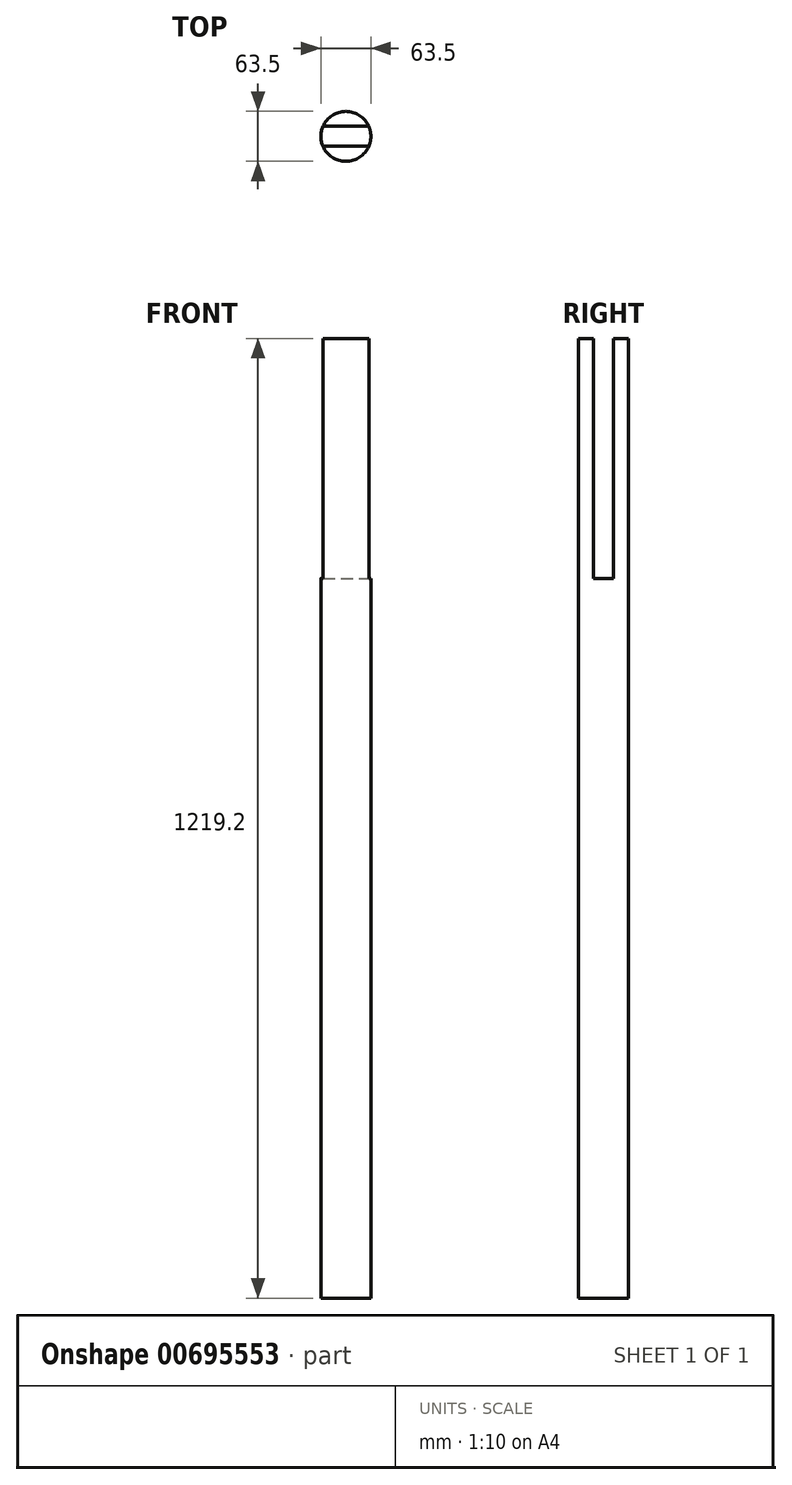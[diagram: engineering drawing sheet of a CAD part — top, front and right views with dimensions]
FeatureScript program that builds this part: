
annotation { "Feature Type Name" : "Feature", "Feature Type Description" : "" }
export const myFeature = defineFeature(function(context is Context, id is Id, definition is map)
    precondition{}
    {
        {
            var Q0;
            Q0=qCreatedBy(makeId("Top.planeOp"),FACE);
            var sketch = newSketch(context, id + "F0", { "sketchPlane" : qUnion([Q0])});
            skCircle(sketch, "E0", {"center": v(0, 0) * mm, "radius": 31.75 * mm});
            skSolve(sketch);
        }
        {
            var Q0;
            Q0 = qSketchRegion(id + "F0", true);
            extrude(context, id + "F1", {"entities" : qUnion([Q0]), "endBound" : BoundingType.SYMMETRIC, "oppositeDirection" : true, "depth" : 1219.2 * mm, "offsetDistance" : 25.4 * mm});
        }
        {
            var Q0;
            Q0=makeQuery(id+"F1.opExtrude","CAP_FACE",FACE,{"disambiguationData":[OSD([sQuery(id+"F0.wireOp",EDGE,"E0")])],"isStart":true});
            var sketch = newSketch(context, id + "F2", { "sketchPlane" : qUnion([Q0])});
            skLineSegment(sketch, "E1.bottom", {"start": v(-29.1, 12.7) * mm, "end": v(29.1, 12.7) * mm});
            skLineSegment(sketch, "E1.top", {"start": v(-29.1, -12.7) * mm, "end": v(29.1, -12.7) * mm});
            skPoint(sketch, "E1.middle", {"position": v(0, 0) * mm});
            skArc(sketch, "E2", {"start": v(-29.1, 12.7) * mm, "mid": v(-31.75, 0) * mm, "end": v(-29.1, -12.7) * mm});
            skPoint(sketch, "E1.left.start.orphan", {"position": v(-50.8, 12.7) * mm});
            skPoint(sketch, "E3.orphan", {"position": v(-50.8, -12.7) * mm});
            skArc(sketch, "E4.trimOffspring", {"start": v(29.1, -12.7) * mm, "mid": v(31.75, 0) * mm, "end": v(29.1, 12.7) * mm});
            skPoint(sketch, "E1.right.start.orphan", {"position": v(50.8, 12.7) * mm});
            skPoint(sketch, "E5.orphan", {"position": v(50.8, -12.7) * mm});
            skSolve(sketch);
        }
        {
            var Q0;
            Q0 = qSketchRegion(id + "F2", true);
            extrude(context, id + "F3", {"entities" : qUnion([Q0]), "operationType" : NewBodyOperationType.REMOVE, "oppositeDirection" : true, "depth" : 304.8 * mm, "offsetDistance" : 25.4 * mm});
        }
    });
